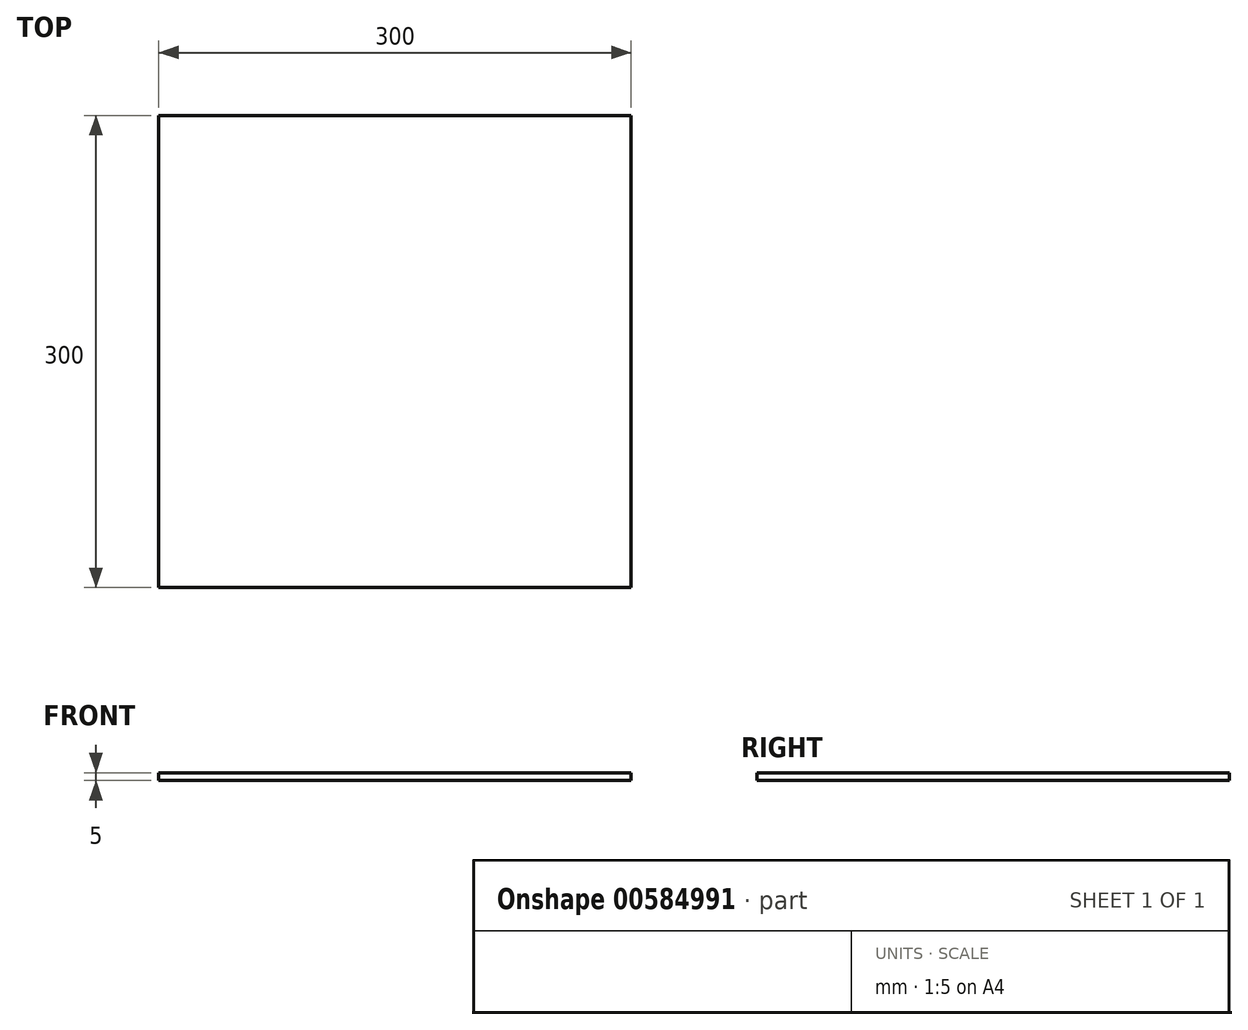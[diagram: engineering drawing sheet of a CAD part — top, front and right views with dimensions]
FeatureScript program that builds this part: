
annotation { "Feature Type Name" : "Feature", "Feature Type Description" : "" }
export const myFeature = defineFeature(function(context is Context, id is Id, definition is map)
    precondition{}
    {
        {
            var Q0;
            Q0=qCreatedBy(makeId("Top.planeOp"),FACE);
            var sketch = newSketch(context, id + "F0", { "sketchPlane" : qUnion([Q0])});
            skLineSegment(sketch, "E0.bottom", {"start": v(-150, 150) * mm, "end": v(150, 150) * mm});
            skLineSegment(sketch, "E0.top", {"start": v(-150, -150) * mm, "end": v(150, -150) * mm});
            skLineSegment(sketch, "E0.left", {"start": v(-150, 150) * mm, "end": v(-150, -150) * mm});
            skLineSegment(sketch, "E0.right", {"start": v(150, 150) * mm, "end": v(150, -150) * mm});
            skPoint(sketch, "E0.middle", {"position": v(0, 0) * mm});
            skLineSegment(sketch, "E1", {"start": v(-335.86, 4.55) * mm, "end": v(-294.57, -35.75) * mm});
            skLineSegment(sketch, "E2", {"start": v(-294.57, -35.75) * mm, "end": v(-241.5, 3.57) * mm});
            skSolve(sketch);
        }
        {
            var Q0;
            Q0 = qSketchRegion(id + "F0", true);
            extrude(context, id + "F1", {"entities" : qUnion([Q0]), "depth" : 5 * mm, "offsetDistance" : 25 * mm});
        }
    });
